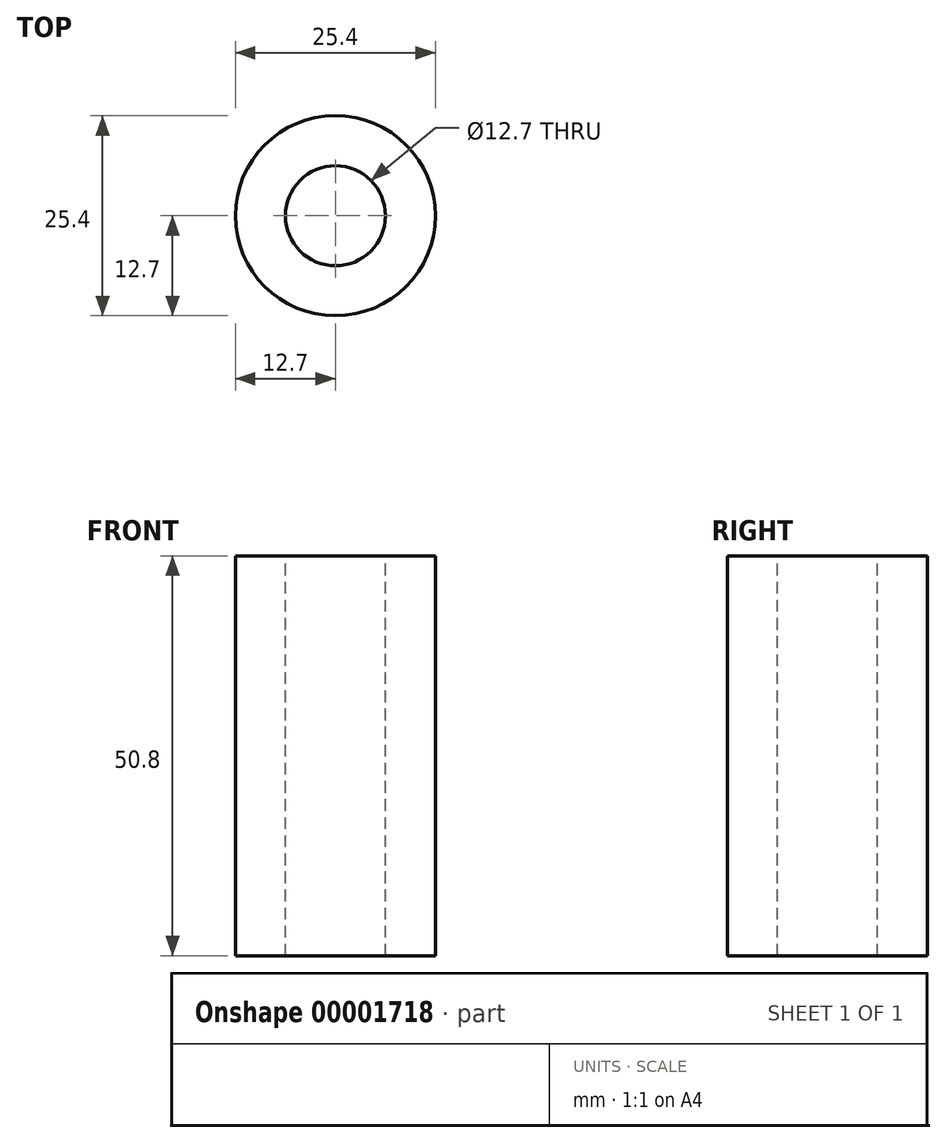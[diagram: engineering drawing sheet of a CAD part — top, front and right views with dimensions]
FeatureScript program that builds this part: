
annotation { "Feature Type Name" : "Feature", "Feature Type Description" : "" }
export const myFeature = defineFeature(function(context is Context, id is Id, definition is map)
    precondition{}
    {
        {
            var Q0;
            Q0=qCreatedBy(makeId("Top.planeOp"),FACE);
            var sketch = newSketch(context, id + "F0", { "sketchPlane" : qUnion([Q0])});
            skCircle(sketch, "E0", {"center": v(0, 0) * mm, "radius": 12.7 * mm});
            skSolve(sketch);
        }
        {
            var Q0;
            Q0 = qSketchRegion(id + "F0", true);
            extrude(context, id + "F1", {"entities" : qUnion([Q0]), "depth" : 50.8 * mm});
        }
        {
            var Q0;
            Q0=makeQuery(id+"F1.opExtrude","CAP_FACE",FACE,{"disambiguationData":[OSD([sQuery(id+"F0.wireOp",EDGE,"E0")])],"isStart":false});
            var sketch = newSketch(context, id + "F2", { "sketchPlane" : qUnion([Q0])});
            skCircle(sketch, "E1", {"center": v(0, 0) * mm, "radius": 6.35 * mm});
            skSolve(sketch);
        }
        {
            var Q0;
            Q0 = qSketchRegion(id + "F2", true);
            extrude(context, id + "F3", {"entities" : qUnion([Q0]), "operationType" : NewBodyOperationType.REMOVE, "endBound" : BoundingType.THROUGH_ALL, "oppositeDirection" : true, "depth" : 25.4 * mm});
        }
    });
